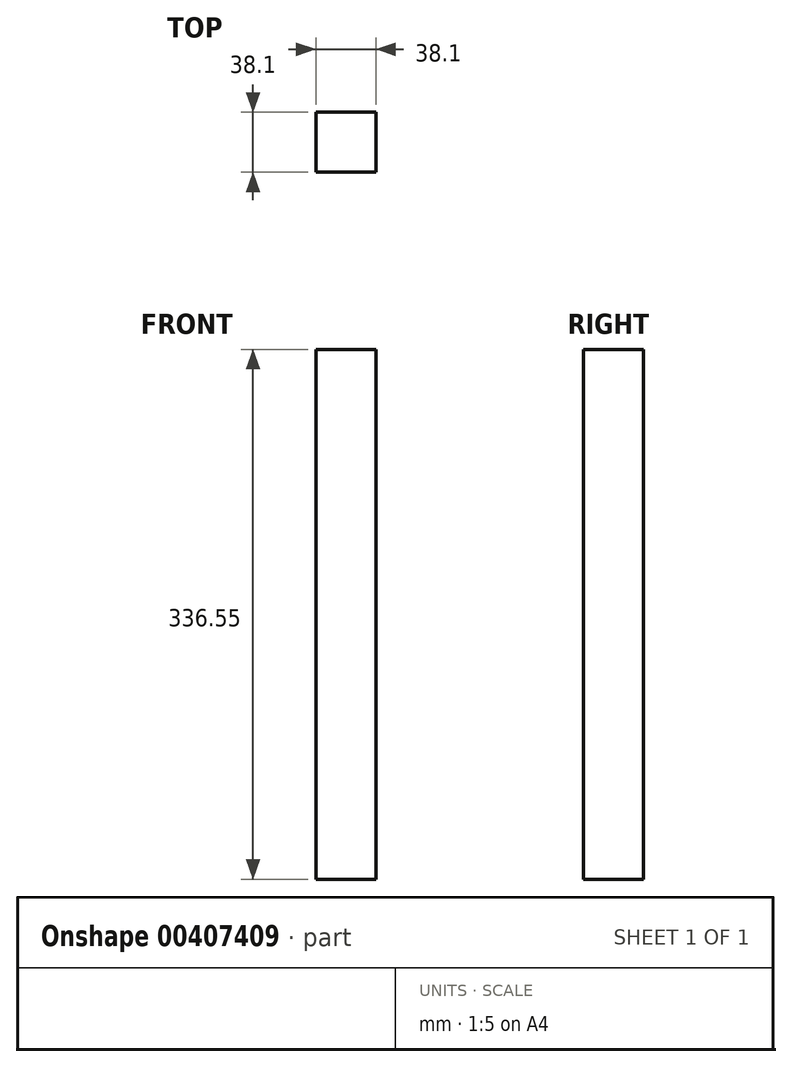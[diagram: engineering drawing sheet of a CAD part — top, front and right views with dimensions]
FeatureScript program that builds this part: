
annotation { "Feature Type Name" : "Feature", "Feature Type Description" : "" }
export const myFeature = defineFeature(function(context is Context, id is Id, definition is map)
    precondition{}
    {
        {
            var Q0;
            Q0=qCreatedBy(makeId("Top.planeOp"),FACE);
            var sketch = newSketch(context, id + "F0", { "sketchPlane" : qUnion([Q0])});
            skLineSegment(sketch, "E0.bottom", {"start": v(19.05, 19.05) * mm, "end": v(-19.05, 19.05) * mm});
            skLineSegment(sketch, "E0.top", {"start": v(19.05, -19.05) * mm, "end": v(-19.05, -19.05) * mm});
            skLineSegment(sketch, "E0.left", {"start": v(19.05, 19.05) * mm, "end": v(19.05, -19.05) * mm});
            skLineSegment(sketch, "E0.right", {"start": v(-19.05, 19.05) * mm, "end": v(-19.05, -19.05) * mm});
            skPoint(sketch, "E0.middle", {"position": v(0, 0) * mm});
            skSolve(sketch);
        }
        {
            var Q0;
            Q0=makeQuery(id+"F0.imprint","IMPRINT",FACE,{"disambiguationData":[TD([[makeQuery(id+"F0.imprint","IMPRINT",EDGE,{"derivedFrom":sQuery(id+"F0.wireOp",EDGE,"E0.bottom")}),1.0]])]});
            extrude(context, id + "F1", {"entities" : qUnion([Q0]), "depth" : 336.55 * mm});
        }
    });
